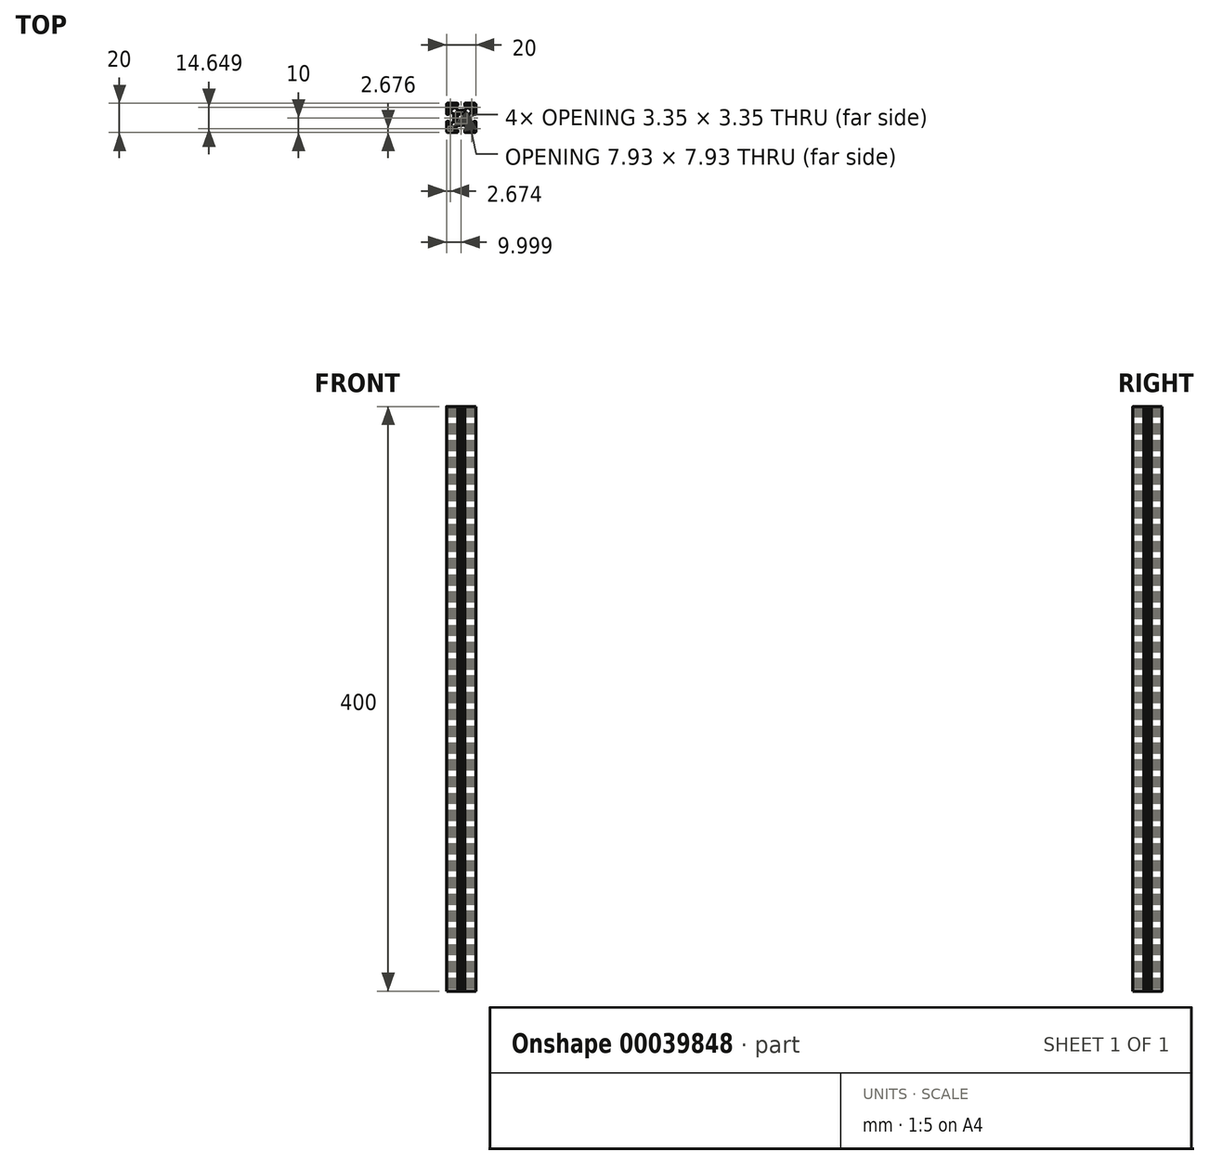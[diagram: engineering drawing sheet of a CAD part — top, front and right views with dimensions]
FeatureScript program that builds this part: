
annotation { "Feature Type Name" : "Feature", "Feature Type Description" : "" }
export const myFeature = defineFeature(function(context is Context, id is Id, definition is map)
    precondition{}
    {
        {
            var Q0;
            Q0=qCreatedBy(makeId("Top.planeOp"),FACE);
            var sketch = newSketch(context, id + "F0", { "sketchPlane" : qUnion([Q0])});
            skLineSegment(sketch, "E0", {"start": v(-770.66, 200.22) * mm, "end": v(-777.22, 200.22) * mm});
            skLineSegment(sketch, "E1", {"start": v(-770.66, 180.22) * mm, "end": v(-777.22, 180.22) * mm});
            skLineSegment(sketch, "E2", {"start": v(-769.86, 199.42) * mm, "end": v(-769.86, 192.86) * mm});
            skLineSegment(sketch, "E3", {"start": v(-789.86, 199.42) * mm, "end": v(-789.86, 192.86) * mm});
            skLineSegment(sketch, "E4", {"start": v(-777.5, 195.42) * mm, "end": v(-779.34, 195.42) * mm});
            skLineSegment(sketch, "E5", {"start": v(-781.86, 195.42) * mm, "end": v(-782.21, 195.42) * mm});
            skArc(sketch, "E6", {"start": v(-777.22, 200.22) * mm, "mid": v(-777.39, 200.15) * mm, "end": v(-777.46, 199.98) * mm});
            skLineSegment(sketch, "E7", {"start": v(-775.06, 198.62) * mm, "end": v(-777.22, 198.62) * mm});
            skArc(sketch, "E8", {"start": v(-777.46, 198.86) * mm, "mid": v(-777.39, 198.7) * mm, "end": v(-777.22, 198.62) * mm});
            skLineSegment(sketch, "E9", {"start": v(-782.5, 198.62) * mm, "end": v(-784.66, 198.62) * mm});
            skArc(sketch, "E10", {"start": v(-782.5, 198.62) * mm, "mid": v(-782.33, 198.7) * mm, "end": v(-782.26, 198.86) * mm});
            skLineSegment(sketch, "E11", {"start": v(-784.66, 197.87) * mm, "end": v(-784.66, 198.62) * mm});
            skLineSegment(sketch, "E12", {"start": v(-775.06, 197.87) * mm, "end": v(-775.06, 198.62) * mm});
            skLineSegment(sketch, "E13", {"start": v(-782.26, 198.86) * mm, "end": v(-782.26, 199.98) * mm});
            skArc(sketch, "E14", {"start": v(-782.26, 199.98) * mm, "mid": v(-782.33, 200.15) * mm, "end": v(-782.5, 200.22) * mm});
            skLineSegment(sketch, "E15", {"start": v(-777.46, 198.86) * mm, "end": v(-777.46, 199.98) * mm});
            skLineSegment(sketch, "E16", {"start": v(-780.18, 195.37) * mm, "end": v(-779.86, 195.18) * mm});
            skLineSegment(sketch, "E17", {"start": v(-779.54, 195.37) * mm, "end": v(-779.86, 195.18) * mm});
            skArc(sketch, "E18", {"start": v(-779.34, 195.42) * mm, "mid": v(-779.44, 195.4) * mm, "end": v(-779.54, 195.37) * mm});
            skLineSegment(sketch, "E19", {"start": v(-782.21, 195.42) * mm, "end": v(-784.66, 197.87) * mm});
            skLineSegment(sketch, "E20", {"start": v(-777.5, 195.42) * mm, "end": v(-775.06, 197.87) * mm});
            skLineSegment(sketch, "E21", {"start": v(-781.86, 195.42) * mm, "end": v(-780.83, 195.22) * mm});
            skArc(sketch, "E22", {"start": v(-780.18, 195.37) * mm, "mid": v(-780.38, 195.42) * mm, "end": v(-780.58, 195.37) * mm});
            skLineSegment(sketch, "E23", {"start": v(-780.58, 195.37) * mm, "end": v(-780.83, 195.22) * mm});
            skLineSegment(sketch, "E24", {"start": v(-777.5, 185.02) * mm, "end": v(-777.86, 185.02) * mm});
            skLineSegment(sketch, "E25", {"start": v(-780.38, 185.02) * mm, "end": v(-782.21, 185.02) * mm});
            skArc(sketch, "E26", {"start": v(-777.46, 180.46) * mm, "mid": v(-777.39, 180.3) * mm, "end": v(-777.22, 180.22) * mm});
            skLineSegment(sketch, "E27", {"start": v(-775.06, 181.82) * mm, "end": v(-777.22, 181.82) * mm});
            skArc(sketch, "E28", {"start": v(-777.22, 181.82) * mm, "mid": v(-777.39, 181.75) * mm, "end": v(-777.46, 181.58) * mm});
            skLineSegment(sketch, "E29", {"start": v(-782.5, 181.82) * mm, "end": v(-784.66, 181.82) * mm});
            skArc(sketch, "E30", {"start": v(-782.26, 181.58) * mm, "mid": v(-782.33, 181.75) * mm, "end": v(-782.5, 181.82) * mm});
            skLineSegment(sketch, "E31", {"start": v(-784.66, 182.57) * mm, "end": v(-784.66, 181.82) * mm});
            skLineSegment(sketch, "E32", {"start": v(-775.06, 182.57) * mm, "end": v(-775.06, 181.82) * mm});
            skLineSegment(sketch, "E33", {"start": v(-782.26, 181.58) * mm, "end": v(-782.26, 180.46) * mm});
            skArc(sketch, "E34", {"start": v(-782.5, 180.22) * mm, "mid": v(-782.33, 180.3) * mm, "end": v(-782.26, 180.46) * mm});
            skLineSegment(sketch, "E35", {"start": v(-777.46, 181.58) * mm, "end": v(-777.46, 180.46) * mm});
            skLineSegment(sketch, "E36", {"start": v(-782.21, 185.02) * mm, "end": v(-784.66, 182.57) * mm});
            skLineSegment(sketch, "E37", {"start": v(-777.5, 185.02) * mm, "end": v(-775.06, 182.57) * mm});
            skLineSegment(sketch, "E38", {"start": v(-779.54, 185.07) * mm, "end": v(-779.86, 185.26) * mm});
            skLineSegment(sketch, "E39", {"start": v(-780.18, 185.07) * mm, "end": v(-779.86, 185.26) * mm});
            skArc(sketch, "E40", {"start": v(-780.38, 185.02) * mm, "mid": v(-780.28, 185.03) * mm, "end": v(-780.18, 185.07) * mm});
            skLineSegment(sketch, "E41", {"start": v(-777.86, 185.02) * mm, "end": v(-778.88, 185.22) * mm});
            skArc(sketch, "E42", {"start": v(-779.54, 185.07) * mm, "mid": v(-779.34, 185.02) * mm, "end": v(-779.14, 185.07) * mm});
            skLineSegment(sketch, "E43", {"start": v(-779.14, 185.07) * mm, "end": v(-778.88, 185.22) * mm});
            skLineSegment(sketch, "E44", {"start": v(-774.66, 187.87) * mm, "end": v(-774.66, 189.7) * mm});
            skLineSegment(sketch, "E45", {"start": v(-774.66, 192.22) * mm, "end": v(-774.66, 192.57) * mm});
            skArc(sketch, "E46", {"start": v(-769.86, 187.58) * mm, "mid": v(-769.93, 187.75) * mm, "end": v(-770.1, 187.82) * mm});
            skLineSegment(sketch, "E47", {"start": v(-771.46, 185.42) * mm, "end": v(-771.46, 187.58) * mm});
            skArc(sketch, "E48", {"start": v(-771.22, 187.82) * mm, "mid": v(-771.39, 187.75) * mm, "end": v(-771.46, 187.58) * mm});
            skLineSegment(sketch, "E49", {"start": v(-771.46, 192.86) * mm, "end": v(-771.46, 195.02) * mm});
            skArc(sketch, "E50", {"start": v(-771.46, 192.86) * mm, "mid": v(-771.39, 192.7) * mm, "end": v(-771.22, 192.62) * mm});
            skLineSegment(sketch, "E51", {"start": v(-772.21, 195.02) * mm, "end": v(-771.46, 195.02) * mm});
            skLineSegment(sketch, "E52", {"start": v(-772.21, 185.42) * mm, "end": v(-771.46, 185.42) * mm});
            skLineSegment(sketch, "E53", {"start": v(-771.22, 192.62) * mm, "end": v(-770.1, 192.62) * mm});
            skArc(sketch, "E54", {"start": v(-770.1, 192.62) * mm, "mid": v(-769.93, 192.7) * mm, "end": v(-769.86, 192.86) * mm});
            skLineSegment(sketch, "E55", {"start": v(-771.22, 187.82) * mm, "end": v(-770.1, 187.82) * mm});
            skLineSegment(sketch, "E56", {"start": v(-774.66, 192.57) * mm, "end": v(-772.21, 195.02) * mm});
            skLineSegment(sketch, "E57", {"start": v(-774.66, 187.87) * mm, "end": v(-772.21, 185.42) * mm});
            skLineSegment(sketch, "E58", {"start": v(-774.71, 190.54) * mm, "end": v(-774.9, 190.22) * mm});
            skLineSegment(sketch, "E59", {"start": v(-774.71, 189.9) * mm, "end": v(-774.9, 190.22) * mm});
            skArc(sketch, "E60", {"start": v(-774.66, 189.7) * mm, "mid": v(-774.67, 189.8) * mm, "end": v(-774.71, 189.9) * mm});
            skLineSegment(sketch, "E61", {"start": v(-774.66, 192.22) * mm, "end": v(-774.86, 191.2) * mm});
            skArc(sketch, "E62", {"start": v(-774.71, 190.54) * mm, "mid": v(-774.66, 190.74) * mm, "end": v(-774.71, 190.94) * mm});
            skLineSegment(sketch, "E63", {"start": v(-774.71, 190.94) * mm, "end": v(-774.86, 191.2) * mm});
            skArc(sketch, "E64", {"start": v(-778.63, 192.65) * mm, "mid": v(-779.86, 192.94) * mm, "end": v(-781.09, 192.65) * mm});
            skArc(sketch, "E65", {"start": v(-782.29, 191.45) * mm, "mid": v(-782.58, 190.22) * mm, "end": v(-782.29, 188.99) * mm});
            skArc(sketch, "E66", {"start": v(-781.09, 187.8) * mm, "mid": v(-779.86, 187.5) * mm, "end": v(-778.63, 187.8) * mm});
            skArc(sketch, "E67", {"start": v(-778.35, 187.75) * mm, "mid": v(-778.48, 187.82) * mm, "end": v(-778.63, 187.8) * mm});
            skArc(sketch, "E68", {"start": v(-778.63, 192.65) * mm, "mid": v(-778.48, 192.62) * mm, "end": v(-778.35, 192.69) * mm});
            skArc(sketch, "E69", {"start": v(-777.43, 188.99) * mm, "mid": v(-777.14, 190.22) * mm, "end": v(-777.43, 191.45) * mm});
            skArc(sketch, "E70", {"start": v(-777.43, 188.99) * mm, "mid": v(-777.46, 188.84) * mm, "end": v(-777.39, 188.71) * mm});
            skArc(sketch, "E71", {"start": v(-777.39, 191.73) * mm, "mid": v(-777.46, 191.6) * mm, "end": v(-777.43, 191.45) * mm});
            skLineSegment(sketch, "E72", {"start": v(-777.39, 191.73) * mm, "end": v(-777, 192.12) * mm});
            skLineSegment(sketch, "E73", {"start": v(-778.35, 192.69) * mm, "end": v(-777.95, 193.09) * mm});
            skLineSegment(sketch, "E74", {"start": v(-778.35, 187.75) * mm, "end": v(-777.95, 187.35) * mm});
            skLineSegment(sketch, "E75", {"start": v(-777.39, 188.71) * mm, "end": v(-777, 188.32) * mm});
            skArc(sketch, "E76", {"start": v(-777, 192.12) * mm, "mid": v(-776.18, 193.9) * mm, "end": v(-777.95, 193.09) * mm});
            skArc(sketch, "E77", {"start": v(-777.95, 187.35) * mm, "mid": v(-776.18, 186.54) * mm, "end": v(-777, 188.32) * mm});
            skArc(sketch, "E78", {"start": v(-781.09, 187.8) * mm, "mid": v(-781.24, 187.82) * mm, "end": v(-781.37, 187.75) * mm});
            skArc(sketch, "E79", {"start": v(-781.37, 192.69) * mm, "mid": v(-781.24, 192.62) * mm, "end": v(-781.09, 192.65) * mm});
            skArc(sketch, "E80", {"start": v(-782.33, 188.71) * mm, "mid": v(-782.26, 188.84) * mm, "end": v(-782.29, 188.99) * mm});
            skArc(sketch, "E81", {"start": v(-782.29, 191.45) * mm, "mid": v(-782.26, 191.6) * mm, "end": v(-782.33, 191.73) * mm});
            skLineSegment(sketch, "E82", {"start": v(-782.33, 191.73) * mm, "end": v(-782.73, 192.12) * mm});
            skLineSegment(sketch, "E83", {"start": v(-781.37, 187.75) * mm, "end": v(-781.76, 187.35) * mm});
            skLineSegment(sketch, "E84", {"start": v(-782.33, 188.71) * mm, "end": v(-782.73, 188.32) * mm});
            skArc(sketch, "E85", {"start": v(-781.76, 193.09) * mm, "mid": v(-783.54, 193.9) * mm, "end": v(-782.73, 192.12) * mm});
            skArc(sketch, "E86", {"start": v(-782.73, 188.32) * mm, "mid": v(-783.54, 186.54) * mm, "end": v(-781.76, 187.35) * mm});
            skLineSegment(sketch, "E87", {"start": v(-781.37, 192.69) * mm, "end": v(-781.76, 193.09) * mm});
            skLineSegment(sketch, "E88", {"start": v(-773.87, 198.26) * mm, "end": v(-773.41, 197.8) * mm});
            skLineSegment(sketch, "E89", {"start": v(-772.28, 196.67) * mm, "end": v(-771.82, 196.2) * mm});
            skLineSegment(sketch, "E90", {"start": v(-770.86, 198.02) * mm, "end": v(-770.86, 196.6) * mm});
            skLineSegment(sketch, "E91", {"start": v(-772.06, 199.22) * mm, "end": v(-773.48, 199.22) * mm});
            skArc(sketch, "E92", {"start": v(-770.86, 198.02) * mm, "mid": v(-771.21, 198.87) * mm, "end": v(-772.06, 199.22) * mm});
            skLineSegment(sketch, "E93", {"start": v(-773.41, 197.8) * mm, "end": v(-773.98, 197.23) * mm});
            skLineSegment(sketch, "E94", {"start": v(-772.28, 196.67) * mm, "end": v(-772.84, 196.1) * mm});
            skArc(sketch, "E95", {"start": v(-773.98, 197.23) * mm, "mid": v(-773.98, 196.1) * mm, "end": v(-772.84, 196.1) * mm});
            skArc(sketch, "E96", {"start": v(-771.82, 196.2) * mm, "mid": v(-771.2, 196.08) * mm, "end": v(-770.86, 196.6) * mm});
            skArc(sketch, "E97", {"start": v(-773.48, 199.22) * mm, "mid": v(-774, 198.87) * mm, "end": v(-773.87, 198.26) * mm});
            skLineSegment(sketch, "E98", {"start": v(-773.87, 182.18) * mm, "end": v(-773.41, 182.64) * mm});
            skLineSegment(sketch, "E99", {"start": v(-772.28, 183.77) * mm, "end": v(-771.82, 184.23) * mm});
            skLineSegment(sketch, "E100", {"start": v(-770.86, 182.42) * mm, "end": v(-770.86, 183.84) * mm});
            skLineSegment(sketch, "E101", {"start": v(-772.06, 181.22) * mm, "end": v(-773.48, 181.22) * mm});
            skArc(sketch, "E102", {"start": v(-772.06, 181.22) * mm, "mid": v(-771.21, 181.57) * mm, "end": v(-770.86, 182.42) * mm});
            skLineSegment(sketch, "E103", {"start": v(-773.41, 182.64) * mm, "end": v(-773.98, 183.2) * mm});
            skLineSegment(sketch, "E104", {"start": v(-772.28, 183.77) * mm, "end": v(-772.84, 184.34) * mm});
            skArc(sketch, "E105", {"start": v(-772.84, 184.34) * mm, "mid": v(-773.98, 184.34) * mm, "end": v(-773.98, 183.2) * mm});
            skArc(sketch, "E106", {"start": v(-770.86, 183.84) * mm, "mid": v(-771.2, 184.36) * mm, "end": v(-771.82, 184.23) * mm});
            skArc(sketch, "E107", {"start": v(-773.87, 182.18) * mm, "mid": v(-774, 181.57) * mm, "end": v(-773.48, 181.22) * mm});
            skLineSegment(sketch, "E108", {"start": v(-785.06, 187.87) * mm, "end": v(-785.06, 188.22) * mm});
            skLineSegment(sketch, "E109", {"start": v(-785.06, 190.74) * mm, "end": v(-785.06, 192.57) * mm});
            skArc(sketch, "E110", {"start": v(-789.62, 187.82) * mm, "mid": v(-789.79, 187.75) * mm, "end": v(-789.86, 187.58) * mm});
            skLineSegment(sketch, "E111", {"start": v(-788.26, 185.42) * mm, "end": v(-788.26, 187.58) * mm});
            skArc(sketch, "E112", {"start": v(-788.26, 187.58) * mm, "mid": v(-788.33, 187.75) * mm, "end": v(-788.5, 187.82) * mm});
            skLineSegment(sketch, "E113", {"start": v(-788.26, 192.86) * mm, "end": v(-788.26, 195.02) * mm});
            skArc(sketch, "E114", {"start": v(-788.5, 192.62) * mm, "mid": v(-788.33, 192.7) * mm, "end": v(-788.26, 192.86) * mm});
            skLineSegment(sketch, "E115", {"start": v(-787.5, 195.02) * mm, "end": v(-788.26, 195.02) * mm});
            skLineSegment(sketch, "E116", {"start": v(-787.5, 185.42) * mm, "end": v(-788.26, 185.42) * mm});
            skLineSegment(sketch, "E117", {"start": v(-788.5, 192.62) * mm, "end": v(-789.62, 192.62) * mm});
            skArc(sketch, "E118", {"start": v(-789.86, 192.86) * mm, "mid": v(-789.79, 192.7) * mm, "end": v(-789.62, 192.62) * mm});
            skLineSegment(sketch, "E119", {"start": v(-788.5, 187.82) * mm, "end": v(-789.62, 187.82) * mm});
            skLineSegment(sketch, "E120", {"start": v(-785.06, 192.57) * mm, "end": v(-787.5, 195.02) * mm});
            skLineSegment(sketch, "E121", {"start": v(-785.06, 187.87) * mm, "end": v(-787.5, 185.42) * mm});
            skLineSegment(sketch, "E122", {"start": v(-785, 189.9) * mm, "end": v(-784.82, 190.22) * mm});
            skLineSegment(sketch, "E123", {"start": v(-785, 190.54) * mm, "end": v(-784.82, 190.22) * mm});
            skArc(sketch, "E124", {"start": v(-785.06, 190.74) * mm, "mid": v(-785.05, 190.64) * mm, "end": v(-785, 190.54) * mm});
            skLineSegment(sketch, "E125", {"start": v(-785.06, 188.22) * mm, "end": v(-784.86, 189.24) * mm});
            skArc(sketch, "E126", {"start": v(-785, 189.9) * mm, "mid": v(-785.06, 189.7) * mm, "end": v(-785, 189.5) * mm});
            skLineSegment(sketch, "E127", {"start": v(-785, 189.5) * mm, "end": v(-784.86, 189.24) * mm});
            skLineSegment(sketch, "E128", {"start": v(-769.86, 187.58) * mm, "end": v(-769.86, 181.02) * mm});
            skLineSegment(sketch, "E129", {"start": v(-782.5, 200.22) * mm, "end": v(-789.06, 200.22) * mm});
            skLineSegment(sketch, "E130", {"start": v(-789.86, 187.58) * mm, "end": v(-789.86, 181.02) * mm});
            skLineSegment(sketch, "E131", {"start": v(-782.5, 180.22) * mm, "end": v(-789.06, 180.22) * mm});
            skLineSegment(sketch, "E132", {"start": v(-785.84, 198.26) * mm, "end": v(-786.3, 197.8) * mm});
            skLineSegment(sketch, "E133", {"start": v(-787.44, 196.67) * mm, "end": v(-787.9, 196.2) * mm});
            skLineSegment(sketch, "E134", {"start": v(-788.86, 198.02) * mm, "end": v(-788.86, 196.6) * mm});
            skLineSegment(sketch, "E135", {"start": v(-787.66, 199.22) * mm, "end": v(-786.24, 199.22) * mm});
            skArc(sketch, "E136", {"start": v(-787.66, 199.22) * mm, "mid": v(-788.5, 198.87) * mm, "end": v(-788.86, 198.02) * mm});
            skLineSegment(sketch, "E137", {"start": v(-786.3, 197.8) * mm, "end": v(-785.74, 197.23) * mm});
            skLineSegment(sketch, "E138", {"start": v(-787.44, 196.67) * mm, "end": v(-786.87, 196.1) * mm});
            skArc(sketch, "E139", {"start": v(-786.87, 196.1) * mm, "mid": v(-785.74, 196.1) * mm, "end": v(-785.74, 197.23) * mm});
            skArc(sketch, "E140", {"start": v(-788.86, 196.6) * mm, "mid": v(-788.51, 196.08) * mm, "end": v(-787.9, 196.2) * mm});
            skArc(sketch, "E141", {"start": v(-785.84, 198.26) * mm, "mid": v(-785.72, 198.87) * mm, "end": v(-786.24, 199.22) * mm});
            skLineSegment(sketch, "E142", {"start": v(-785.84, 182.18) * mm, "end": v(-786.3, 182.64) * mm});
            skLineSegment(sketch, "E143", {"start": v(-787.44, 183.77) * mm, "end": v(-787.9, 184.23) * mm});
            skLineSegment(sketch, "E144", {"start": v(-788.86, 182.42) * mm, "end": v(-788.86, 183.84) * mm});
            skLineSegment(sketch, "E145", {"start": v(-787.66, 181.22) * mm, "end": v(-786.24, 181.22) * mm});
            skArc(sketch, "E146", {"start": v(-788.86, 182.42) * mm, "mid": v(-788.5, 181.57) * mm, "end": v(-787.66, 181.22) * mm});
            skLineSegment(sketch, "E147", {"start": v(-786.3, 182.64) * mm, "end": v(-785.74, 183.2) * mm});
            skLineSegment(sketch, "E148", {"start": v(-787.44, 183.77) * mm, "end": v(-786.87, 184.34) * mm});
            skArc(sketch, "E149", {"start": v(-785.74, 183.2) * mm, "mid": v(-785.74, 184.34) * mm, "end": v(-786.87, 184.34) * mm});
            skArc(sketch, "E150", {"start": v(-787.9, 184.23) * mm, "mid": v(-788.51, 184.36) * mm, "end": v(-788.86, 183.84) * mm});
            skArc(sketch, "E151", {"start": v(-786.24, 181.22) * mm, "mid": v(-785.72, 181.57) * mm, "end": v(-785.84, 182.18) * mm});
            skArc(sketch, "E152", {"start": v(-769.86, 199.42) * mm, "mid": v(-770.1, 199.99) * mm, "end": v(-770.66, 200.22) * mm});
            skArc(sketch, "E153", {"start": v(-770.66, 180.22) * mm, "mid": v(-770.1, 180.45) * mm, "end": v(-769.86, 181.02) * mm});
            skArc(sketch, "E154", {"start": v(-789.86, 181.02) * mm, "mid": v(-789.62, 180.45) * mm, "end": v(-789.06, 180.22) * mm});
            skArc(sketch, "E155", {"start": v(-789.06, 200.22) * mm, "mid": v(-789.62, 199.99) * mm, "end": v(-789.86, 199.42) * mm});
            skCircle(sketch, "E156", {"center": v(-779.86, 190.22) * mm, "radius": 2.72 * mm});
            skSolve(sketch);
        }
        {
            var Q0;
            Q0=makeQuery(id+"F0.imprint","IMPRINT",FACE,{"disambiguationData":[TD([[makeQuery(id+"F0.imprint","IMPRINT",EDGE,{"derivedFrom":sQuery(id+"F0.wireOp",EDGE,"E0")}),1.0]])]});
            extrude(context, id + "F1", {"entities" : qUnion([Q0]), "depth" : 400 * mm});
        }
        {
            var Q0;
            Q0=makeQuery(id+"F1.opExtrude","SWEPT_BODY",BODY,{"disambiguationData":[OSD([sQuery(id+"F0.wireOp",EDGE,"E0"),sQuery(id+"F0.wireOp",EDGE,"E1"),sQuery(id+"F0.wireOp",EDGE,"E2"),sQuery(id+"F0.wireOp",EDGE,"E3"),sQuery(id+"F0.wireOp",EDGE,"E4"),sQuery(id+"F0.wireOp",EDGE,"E5"),sQuery(id+"F0.wireOp",EDGE,"E6"),sQuery(id+"F0.wireOp",EDGE,"E7"),sQuery(id+"F0.wireOp",EDGE,"E8"),sQuery(id+"F0.wireOp",EDGE,"E9"),sQuery(id+"F0.wireOp",EDGE,"E10"),sQuery(id+"F0.wireOp",EDGE,"E11"),sQuery(id+"F0.wireOp",EDGE,"E12"),sQuery(id+"F0.wireOp",EDGE,"E13"),sQuery(id+"F0.wireOp",EDGE,"E14"),sQuery(id+"F0.wireOp",EDGE,"E15"),sQuery(id+"F0.wireOp",EDGE,"E16"),sQuery(id+"F0.wireOp",EDGE,"E17"),sQuery(id+"F0.wireOp",EDGE,"E18"),sQuery(id+"F0.wireOp",EDGE,"E19"),sQuery(id+"F0.wireOp",EDGE,"E20"),sQuery(id+"F0.wireOp",EDGE,"E21"),sQuery(id+"F0.wireOp",EDGE,"E22"),sQuery(id+"F0.wireOp",EDGE,"E23"),sQuery(id+"F0.wireOp",EDGE,"E24"),sQuery(id+"F0.wireOp",EDGE,"E25"),sQuery(id+"F0.wireOp",EDGE,"E26"),sQuery(id+"F0.wireOp",EDGE,"E27"),sQuery(id+"F0.wireOp",EDGE,"E28"),sQuery(id+"F0.wireOp",EDGE,"E29"),sQuery(id+"F0.wireOp",EDGE,"E30"),sQuery(id+"F0.wireOp",EDGE,"E31"),sQuery(id+"F0.wireOp",EDGE,"E32"),sQuery(id+"F0.wireOp",EDGE,"E33"),sQuery(id+"F0.wireOp",EDGE,"E34"),sQuery(id+"F0.wireOp",EDGE,"E35"),sQuery(id+"F0.wireOp",EDGE,"E36"),sQuery(id+"F0.wireOp",EDGE,"E37"),sQuery(id+"F0.wireOp",EDGE,"E38"),sQuery(id+"F0.wireOp",EDGE,"E39"),sQuery(id+"F0.wireOp",EDGE,"E40"),sQuery(id+"F0.wireOp",EDGE,"E41"),sQuery(id+"F0.wireOp",EDGE,"E42"),sQuery(id+"F0.wireOp",EDGE,"E43"),sQuery(id+"F0.wireOp",EDGE,"E44"),sQuery(id+"F0.wireOp",EDGE,"E45"),sQuery(id+"F0.wireOp",EDGE,"E46"),sQuery(id+"F0.wireOp",EDGE,"E47"),sQuery(id+"F0.wireOp",EDGE,"E48"),sQuery(id+"F0.wireOp",EDGE,"E49"),sQuery(id+"F0.wireOp",EDGE,"E50"),sQuery(id+"F0.wireOp",EDGE,"E51"),sQuery(id+"F0.wireOp",EDGE,"E52"),sQuery(id+"F0.wireOp",EDGE,"E53"),sQuery(id+"F0.wireOp",EDGE,"E54"),sQuery(id+"F0.wireOp",EDGE,"E55"),sQuery(id+"F0.wireOp",EDGE,"E56"),sQuery(id+"F0.wireOp",EDGE,"E57"),sQuery(id+"F0.wireOp",EDGE,"E58"),sQuery(id+"F0.wireOp",EDGE,"E59"),sQuery(id+"F0.wireOp",EDGE,"E60"),sQuery(id+"F0.wireOp",EDGE,"E61"),sQuery(id+"F0.wireOp",EDGE,"E62"),sQuery(id+"F0.wireOp",EDGE,"E63"),sQuery(id+"F0.wireOp",EDGE,"E67"),sQuery(id+"F0.wireOp",EDGE,"E68"),sQuery(id+"F0.wireOp",EDGE,"E70"),sQuery(id+"F0.wireOp",EDGE,"E71"),sQuery(id+"F0.wireOp",EDGE,"E72"),sQuery(id+"F0.wireOp",EDGE,"E73"),sQuery(id+"F0.wireOp",EDGE,"E74"),sQuery(id+"F0.wireOp",EDGE,"E75"),sQuery(id+"F0.wireOp",EDGE,"E76"),sQuery(id+"F0.wireOp",EDGE,"E77"),sQuery(id+"F0.wireOp",EDGE,"E78"),sQuery(id+"F0.wireOp",EDGE,"E79"),sQuery(id+"F0.wireOp",EDGE,"E80"),sQuery(id+"F0.wireOp",EDGE,"E81"),sQuery(id+"F0.wireOp",EDGE,"E82"),sQuery(id+"F0.wireOp",EDGE,"E83"),sQuery(id+"F0.wireOp",EDGE,"E84"),sQuery(id+"F0.wireOp",EDGE,"E85"),sQuery(id+"F0.wireOp",EDGE,"E86"),sQuery(id+"F0.wireOp",EDGE,"E87"),sQuery(id+"F0.wireOp",EDGE,"E88"),sQuery(id+"F0.wireOp",EDGE,"E89"),sQuery(id+"F0.wireOp",EDGE,"E90"),sQuery(id+"F0.wireOp",EDGE,"E91"),sQuery(id+"F0.wireOp",EDGE,"E92"),sQuery(id+"F0.wireOp",EDGE,"E93"),sQuery(id+"F0.wireOp",EDGE,"E94"),sQuery(id+"F0.wireOp",EDGE,"E95"),sQuery(id+"F0.wireOp",EDGE,"E96"),sQuery(id+"F0.wireOp",EDGE,"E97"),sQuery(id+"F0.wireOp",EDGE,"E98"),sQuery(id+"F0.wireOp",EDGE,"E99"),sQuery(id+"F0.wireOp",EDGE,"E100"),sQuery(id+"F0.wireOp",EDGE,"E101"),sQuery(id+"F0.wireOp",EDGE,"E102"),sQuery(id+"F0.wireOp",EDGE,"E103"),sQuery(id+"F0.wireOp",EDGE,"E104"),sQuery(id+"F0.wireOp",EDGE,"E105"),sQuery(id+"F0.wireOp",EDGE,"E106"),sQuery(id+"F0.wireOp",EDGE,"E107"),sQuery(id+"F0.wireOp",EDGE,"E108"),sQuery(id+"F0.wireOp",EDGE,"E109"),sQuery(id+"F0.wireOp",EDGE,"E110"),sQuery(id+"F0.wireOp",EDGE,"E111"),sQuery(id+"F0.wireOp",EDGE,"E112"),sQuery(id+"F0.wireOp",EDGE,"E113"),sQuery(id+"F0.wireOp",EDGE,"E114"),sQuery(id+"F0.wireOp",EDGE,"E115"),sQuery(id+"F0.wireOp",EDGE,"E116"),sQuery(id+"F0.wireOp",EDGE,"E117"),sQuery(id+"F0.wireOp",EDGE,"E118"),sQuery(id+"F0.wireOp",EDGE,"E119"),sQuery(id+"F0.wireOp",EDGE,"E120"),sQuery(id+"F0.wireOp",EDGE,"E121"),sQuery(id+"F0.wireOp",EDGE,"E122"),sQuery(id+"F0.wireOp",EDGE,"E123"),sQuery(id+"F0.wireOp",EDGE,"E124"),sQuery(id+"F0.wireOp",EDGE,"E125"),sQuery(id+"F0.wireOp",EDGE,"E126"),sQuery(id+"F0.wireOp",EDGE,"E127"),sQuery(id+"F0.wireOp",EDGE,"E128"),sQuery(id+"F0.wireOp",EDGE,"E129"),sQuery(id+"F0.wireOp",EDGE,"E130"),sQuery(id+"F0.wireOp",EDGE,"E131"),sQuery(id+"F0.wireOp",EDGE,"E132"),sQuery(id+"F0.wireOp",EDGE,"E133"),sQuery(id+"F0.wireOp",EDGE,"E134"),sQuery(id+"F0.wireOp",EDGE,"E135"),sQuery(id+"F0.wireOp",EDGE,"E136"),sQuery(id+"F0.wireOp",EDGE,"E137"),sQuery(id+"F0.wireOp",EDGE,"E138"),sQuery(id+"F0.wireOp",EDGE,"E139"),sQuery(id+"F0.wireOp",EDGE,"E140"),sQuery(id+"F0.wireOp",EDGE,"E141"),sQuery(id+"F0.wireOp",EDGE,"E142"),sQuery(id+"F0.wireOp",EDGE,"E143"),sQuery(id+"F0.wireOp",EDGE,"E144"),sQuery(id+"F0.wireOp",EDGE,"E145"),sQuery(id+"F0.wireOp",EDGE,"E146"),sQuery(id+"F0.wireOp",EDGE,"E147"),sQuery(id+"F0.wireOp",EDGE,"E148"),sQuery(id+"F0.wireOp",EDGE,"E149"),sQuery(id+"F0.wireOp",EDGE,"E150"),sQuery(id+"F0.wireOp",EDGE,"E151"),sQuery(id+"F0.wireOp",EDGE,"E152"),sQuery(id+"F0.wireOp",EDGE,"E153"),sQuery(id+"F0.wireOp",EDGE,"E154"),sQuery(id+"F0.wireOp",EDGE,"E155"),sQuery(id+"F0.wireOp",EDGE,"E156")])]});
            transform(context, id + "F2", {"entities" : qUnion([Q0]), "transformType" : TransformType.TRANSLATION_3D, "dx" : 780.97 * mm, "dy" : -188.54 * mm, "dz" : -211.27 * mm, "makeCopy" : false});
        }
        {
            var Q0;
            Q0=makeQuery(id+"F1.opExtrude","SWEPT_FACE",FACE,{"disambiguationData":[OSD([sQuery(id+"F0.wireOp",EDGE,"E2")])]});
            var sketch = newSketch(context, id + "F3", { "sketchPlane" : qUnion([Q0])});
            skPoint(sketch, "E157.0", {"position": v(11.68, 188.73) * mm});
            skPoint(sketch, "E157.1", {"position": v(-8.32, 188.73) * mm});
            skLineSegment(sketch, "E158", {"start": v(11.68, 188.73) * mm, "end": v(-8.32, 188.73) * mm, "construction": true});
            skLineSegment(sketch, "E159", {"start": v(11.68, 188.73) * mm, "end": v(11.68, 158.73) * mm, "construction": true});
            skLineSegment(sketch, "E160", {"start": v(-8.32, 188.73) * mm, "end": v(-8.32, 158.73) * mm, "construction": true});
            skLineSegment(sketch, "E161", {"start": v(-8.32, 158.73) * mm, "end": v(11.68, 158.73) * mm, "construction": true});
            skPoint(sketch, "E162.0", {"position": v(-8.32, -211.27) * mm});
            skPoint(sketch, "E162.1", {"position": v(11.68, -211.27) * mm});
            skLineSegment(sketch, "E163", {"start": v(-8.32, -211.27) * mm, "end": v(11.68, -211.27) * mm, "construction": true});
            skLineSegment(sketch, "E164", {"start": v(11.68, -211.27) * mm, "end": v(11.68, -181.27) * mm, "construction": true});
            skLineSegment(sketch, "E165", {"start": v(-8.32, -211.27) * mm, "end": v(-8.32, -181.27) * mm, "construction": true});
            skLineSegment(sketch, "E166", {"start": v(-8.32, -181.27) * mm, "end": v(11.68, -181.27) * mm, "construction": true});
            skLineSegment(sketch, "E167", {"start": v(-8.32, 178.73) * mm, "end": v(11.68, 178.73) * mm, "construction": true});
            skLineSegment(sketch, "E168", {"start": v(-8.32, -201.27) * mm, "end": v(11.68, -201.27) * mm, "construction": true});
            skSolve(sketch);
        }
        {
            var Q0;
            Q0=makeQuery(id+"F1.opExtrude","SWEPT_FACE",FACE,{"disambiguationData":[OSD([sQuery(id+"F0.wireOp",EDGE,"E3")])]});
            var sketch = newSketch(context, id + "F4", { "sketchPlane" : qUnion([Q0])});
            skLineSegment(sketch, "E169.0", {"start": v(8.32, -181.27) * mm, "end": v(-11.68, -181.27) * mm, "construction": true});
            skLineSegment(sketch, "E170.0", {"start": v(8.32, 158.73) * mm, "end": v(-11.68, 158.73) * mm, "construction": true});
            skLineSegment(sketch, "E171.0", {"start": v(8.32, 178.73) * mm, "end": v(-11.68, 178.73) * mm, "construction": true});
            skLineSegment(sketch, "E172.0", {"start": v(8.32, -201.27) * mm, "end": v(-11.68, -201.27) * mm, "construction": true});
            skSolve(sketch);
        }
        {
            var Q0;
            Q0=makeQuery(id+"F1.opExtrude","SWEPT_FACE",FACE,{"disambiguationData":[OSD([sQuery(id+"F0.wireOp",EDGE,"E131")])]});
            var sketch = newSketch(context, id + "F5", { "sketchPlane" : qUnion([Q0])});
            skPoint(sketch, "E173.0", {"position": v(-8.9, 158.73) * mm});
            skPoint(sketch, "E173.1", {"position": v(11.1, 158.73) * mm});
            skLineSegment(sketch, "E174", {"start": v(-8.9, 158.73) * mm, "end": v(11.1, 158.73) * mm, "construction": true});
            skPoint(sketch, "E175.0", {"position": v(-8.9, -181.27) * mm});
            skPoint(sketch, "E175.1", {"position": v(11.1, -181.27) * mm});
            skLineSegment(sketch, "E176", {"start": v(11.1, -181.27) * mm, "end": v(-8.9, -181.27) * mm, "construction": true});
            skPoint(sketch, "E177.0", {"position": v(-8.9, -201.27) * mm});
            skPoint(sketch, "E177.1", {"position": v(11.1, -201.27) * mm});
            skLineSegment(sketch, "E178", {"start": v(-8.9, -201.27) * mm, "end": v(11.1, -201.27) * mm, "construction": true});
            skPoint(sketch, "E179.0", {"position": v(-8.9, 178.73) * mm});
            skPoint(sketch, "E179.1", {"position": v(11.1, 178.73) * mm});
            skLineSegment(sketch, "E180", {"start": v(11.1, 178.73) * mm, "end": v(-8.9, 178.73) * mm, "construction": true});
            skSolve(sketch);
        }
        {
            var Q0;
            Q0=makeQuery(id+"F1.opExtrude","SWEPT_FACE",FACE,{"disambiguationData":[OSD([sQuery(id+"F0.wireOp",EDGE,"E0")])]});
            var sketch = newSketch(context, id + "F6", { "sketchPlane" : qUnion([Q0])});
            skLineSegment(sketch, "E181.0", {"start": v(8.9, 158.73) * mm, "end": v(-11.1, 158.73) * mm, "construction": true});
            skPoint(sketch, "E182.0", {"position": v(-11.1, -181.27) * mm});
            skPoint(sketch, "E182.1", {"position": v(8.9, -181.27) * mm});
            skLineSegment(sketch, "E183", {"start": v(-11.1, -181.27) * mm, "end": v(8.9, -181.27) * mm, "construction": true});
            skPoint(sketch, "E184.0", {"position": v(8.9, -201.27) * mm});
            skPoint(sketch, "E184.1", {"position": v(-11.1, -201.27) * mm});
            skLineSegment(sketch, "E185", {"start": v(8.9, -201.27) * mm, "end": v(-11.1, -201.27) * mm, "construction": true});
            skPoint(sketch, "E186.0", {"position": v(8.9, 178.73) * mm});
            skPoint(sketch, "E186.1", {"position": v(-11.1, 178.73) * mm});
            skLineSegment(sketch, "E187", {"start": v(8.9, 178.73) * mm, "end": v(-11.1, 178.73) * mm, "construction": true});
            skSolve(sketch);
        }
    });
